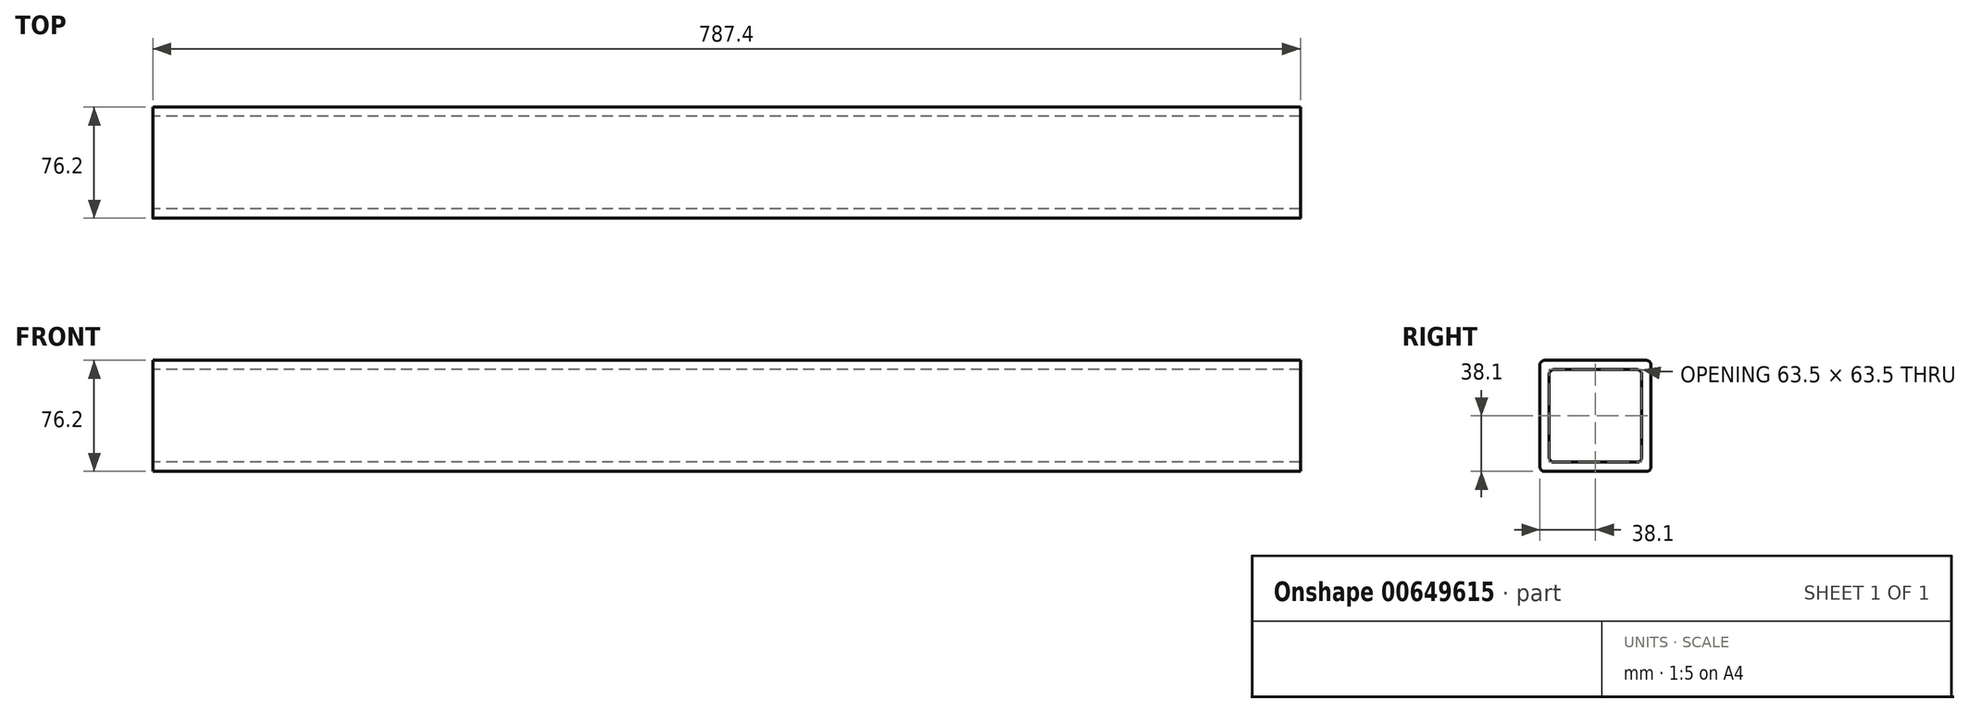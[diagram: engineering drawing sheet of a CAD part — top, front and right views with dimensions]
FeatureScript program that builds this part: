
annotation { "Feature Type Name" : "Feature", "Feature Type Description" : "" }
export const myFeature = defineFeature(function(context is Context, id is Id, definition is map)
    precondition{}
    {
        {
            var Q0;
            Q0=qCreatedBy(makeId("Right.planeOp"),FACE);
            var sketch = newSketch(context, id + "F0", { "sketchPlane" : qUnion([Q0])});
            skLineSegment(sketch, "E0.bottom", {"start": v(34.93, -38.1) * mm, "end": v(-34.93, -38.1) * mm});
            skLineSegment(sketch, "E0.top", {"start": v(34.93, 38.1) * mm, "end": v(-34.93, 38.1) * mm});
            skLineSegment(sketch, "E0.left", {"start": v(38.1, -34.93) * mm, "end": v(38.1, 34.93) * mm});
            skLineSegment(sketch, "E0.right", {"start": v(-38.1, -34.93) * mm, "end": v(-38.1, 34.92) * mm});
            skPoint(sketch, "E0.middle", {"position": v(0, 0) * mm});
            skLineSegment(sketch, "E1.bottom", {"start": v(28.57, -31.75) * mm, "end": v(-28.57, -31.75) * mm});
            skLineSegment(sketch, "E1.top", {"start": v(28.57, 31.75) * mm, "end": v(-28.57, 31.75) * mm});
            skLineSegment(sketch, "E1.left", {"start": v(31.75, -28.57) * mm, "end": v(31.75, 28.57) * mm});
            skLineSegment(sketch, "E1.right", {"start": v(-31.75, -28.57) * mm, "end": v(-31.75, 28.57) * mm});
            skPoint(sketch, "E2.visualSharp", {"position": v(-38.1, 38.1) * mm});
            skArc(sketch, "E2.filletArc", {"start": v(-34.93, 38.1) * mm, "mid": v(-37.17, 37.17) * mm, "end": v(-38.1, 34.92) * mm});
            skPoint(sketch, "E3.visualSharp", {"position": v(-31.75, 31.75) * mm});
            skArc(sketch, "E3.filletArc", {"start": v(-28.57, 31.75) * mm, "mid": v(-30.82, 30.82) * mm, "end": v(-31.75, 28.57) * mm});
            skPoint(sketch, "E4.visualSharp", {"position": v(31.75, 31.75) * mm});
            skArc(sketch, "E4.filletArc", {"start": v(31.75, 28.57) * mm, "mid": v(30.82, 30.82) * mm, "end": v(28.57, 31.75) * mm});
            skPoint(sketch, "E5.visualSharp", {"position": v(38.1, 38.1) * mm});
            skArc(sketch, "E5.filletArc", {"start": v(38.1, 34.93) * mm, "mid": v(37.17, 37.17) * mm, "end": v(34.93, 38.1) * mm});
            skPoint(sketch, "E6.visualSharp", {"position": v(-31.75, -31.75) * mm});
            skArc(sketch, "E6.filletArc", {"start": v(-31.75, -28.57) * mm, "mid": v(-30.82, -30.82) * mm, "end": v(-28.57, -31.75) * mm});
            skPoint(sketch, "E7.visualSharp", {"position": v(31.75, -31.75) * mm});
            skArc(sketch, "E7.filletArc", {"start": v(28.57, -31.75) * mm, "mid": v(30.82, -30.82) * mm, "end": v(31.75, -28.57) * mm});
            skPoint(sketch, "E8.visualSharp", {"position": v(38.1, -38.1) * mm});
            skArc(sketch, "E8.filletArc", {"start": v(34.93, -38.1) * mm, "mid": v(37.17, -37.17) * mm, "end": v(38.1, -34.93) * mm});
            skPoint(sketch, "E9.visualSharp", {"position": v(-38.1, -38.1) * mm});
            skArc(sketch, "E9.filletArc", {"start": v(-38.1, -34.93) * mm, "mid": v(-37.17, -37.17) * mm, "end": v(-34.93, -38.1) * mm});
            skSolve(sketch);
        }
        {
            var Q0;
            Q0 = qSketchRegion(id + "F0", true);
            extrude(context, id + "F1", {"entities" : qUnion([Q0]), "depth" : 787.4 * mm, "offsetDistance" : 25.4 * mm});
        }
    });
